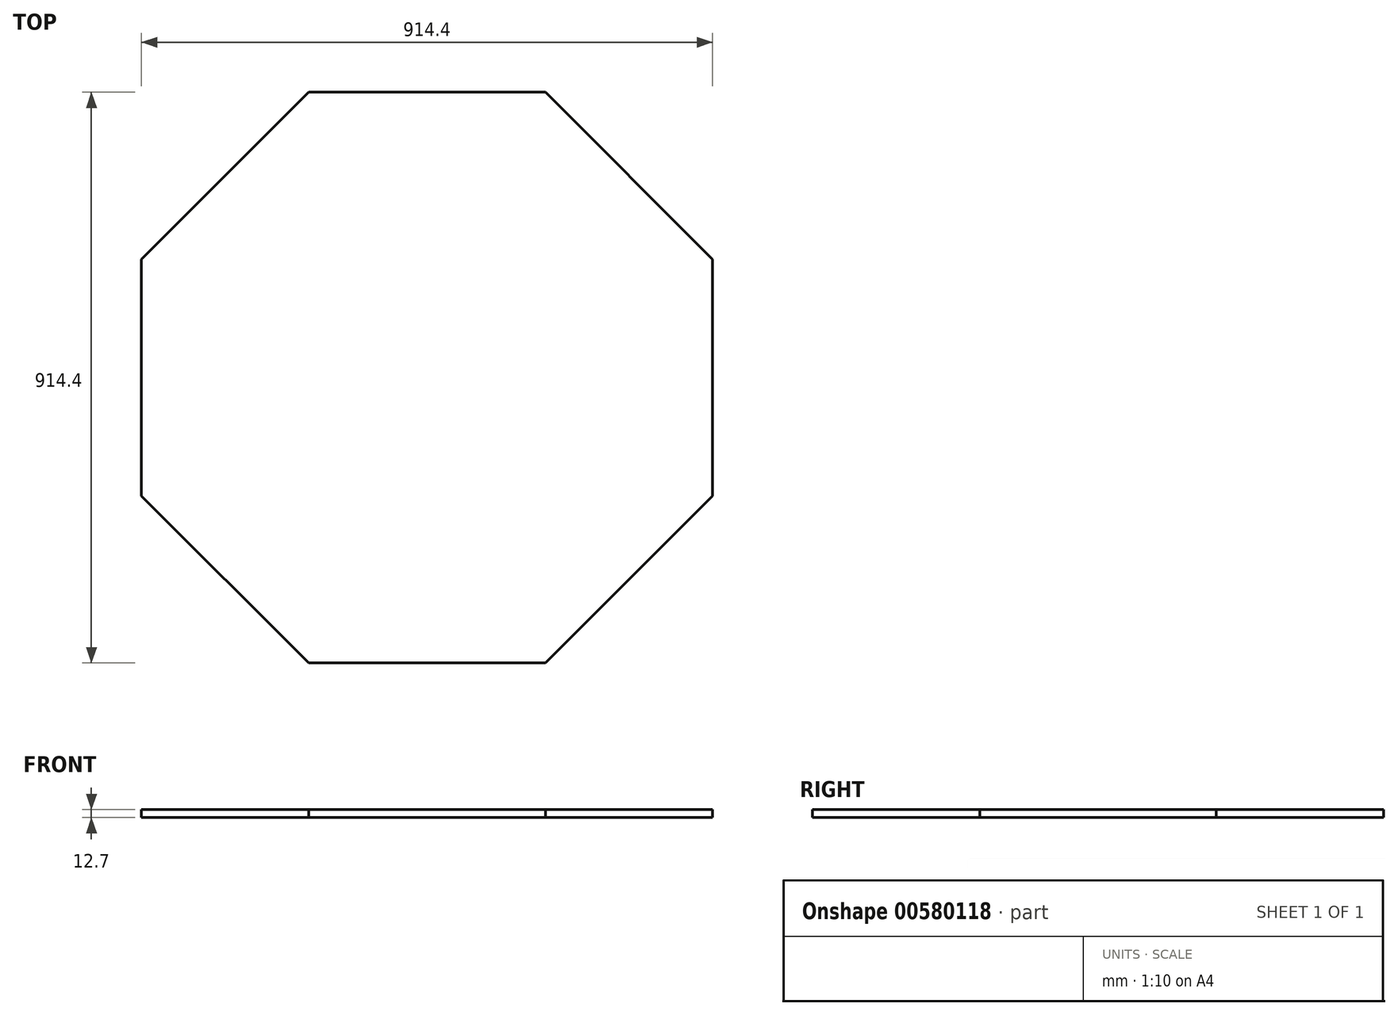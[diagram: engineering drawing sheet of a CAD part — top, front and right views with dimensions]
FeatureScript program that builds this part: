
annotation { "Feature Type Name" : "Feature", "Feature Type Description" : "" }
export const myFeature = defineFeature(function(context is Context, id is Id, definition is map)
    precondition{}
    {
        {
            var Q0;
            Q0=qCreatedBy(makeId("Top.planeOp"),FACE);
            var sketch = newSketch(context, id + "F0", { "sketchPlane" : qUnion([Q0])});
            skCircle(sketch, "E0.cCircle", {"center": v(0, 0) * mm, "radius": 457.2 * mm, "construction": true});
            skLineSegment(sketch, "E0.0", {"start": v(-189.38, 457.2) * mm, "end": v(189.38, 457.2) * mm});
            skLineSegment(sketch, "E0.1", {"start": v(189.38, 457.2) * mm, "end": v(457.2, 189.38) * mm});
            skLineSegment(sketch, "E0.2", {"start": v(457.2, 189.38) * mm, "end": v(457.2, -189.38) * mm});
            skLineSegment(sketch, "E0.3", {"start": v(457.2, -189.38) * mm, "end": v(189.38, -457.2) * mm});
            skLineSegment(sketch, "E0.4", {"start": v(189.38, -457.2) * mm, "end": v(-189.38, -457.2) * mm});
            skLineSegment(sketch, "E0.5", {"start": v(-189.38, -457.2) * mm, "end": v(-457.2, -189.38) * mm});
            skLineSegment(sketch, "E0.6", {"start": v(-457.2, -189.38) * mm, "end": v(-457.2, 189.38) * mm});
            skLineSegment(sketch, "E0.7", {"start": v(-457.2, 189.38) * mm, "end": v(-189.38, 457.2) * mm});
            skPoint(sketch, "E0.0.midPoint", {"position": v(0, 457.2) * mm});
            skSolve(sketch);
        }
        {
            var Q0;
            Q0=qSketchRegion(id+"F0",true);
            extrude(context, id + "F1", {"entities" : qUnion([Q0]), "depth" : 12.7 * mm, "offsetDistance" : 25.4 * mm});
        }
    });
